# Revit family: Мембранный редуктор давления с крышкой фильтрующего элемента из прозрачного пластика 2682
name_source: partatom
category: Rohrzubehör
units: mm (PartAtom-declared; Revit-internal decimal feet)

## family parameters
Arbeitsebenenbasiert = Nein
Beim Laden mit Abzugskörper schneiden = Nein
Bemaßung runder Anschluss = Durchmesser verwenden
Gemeinsam genutzt = Nein
Immer vertikal = Ja
OmniClass-Nummer = 23.65.55.14
OmniClass-Titel = Valves for Liquid Services
Teiletyp = Unterbricht

## types (2) — shared parameters
B02 = 26 mm  [stored 0.0853018 ft]
B03 = 5 mm  [stored 0.0164042 ft]
Hersteller = HERZ Armaturen Ges.m.b.H.
R06 = 19.5 mm  [stored 0.0639764 ft]
S02 = 10 mm  [stored 0.0328084 ft]
SCTWCODE = 04;24;02
SCTWSEQ = AW;SBT_TYP_AW="111";2
URL = www.herz-armaturen.ru
W01 = 91.00°
Букса = PA6.6
Диапазон настройки выходного давления = 1.5 - 6 bar
Заводская настройка давления на выходе = 300000.0 Pa
Корпус (DN15-DN25) = штампованная латунь (EN 12165; CW626N)
Корпус (DN32-DN50) = литая латунь (EN 1982; CC770S)
Крышка = пластик PA12, прозрачный
Макс. давление на входе = 1600000.0 Pa
Макс. рабочая температура = 40 °C
Маховик = пластик PA6.6, зеленого цвета
Мембрана = EPDM
Направляющая пружины = нержавеющая сталь
Наружная резьба подключения = в соответствии с ISO 7-1 и ISO228
Область применения = Мембранный редуктор давления защищает установки от избыточного давления (снижает давление на входе до рабочего уровня).
Редуктор также может использоваться в системах отопления для защиты водонагревателя от высокого давления.
Давление на выходе настраивается в указанном диапазоне и не зависит от изменения давления на входе.
Давление на выходе можно регулировать путем поворота зеленого маховика. 
При повороте маховика по часовой стрелке увеличивается давление на выходе.
Превышение значений, указанных на шкале редуктора, может привести к повреждению устройства.
Для систем в частных домах рекомендуется установить давление на выходе равным 4 бара, что обеспечивает длительный срок службы изделия и низкие затраты во время его эксплуатации.
После изменения настройки необходимо открыть и затем закрыть водоразборный кран и далее проконтролировать достигнутое значение настроенного давления по манометру при закрытом кране водоразбора.
Подключение манометра (с обеих сторон) = 1/4" F (ISO 228-1)
Примечание = В соответствии со статьей 33 Регламента REACH (Registration; Evaluation; Authorisation; Restriction of Chemicals) (EC № 1907/2006) мы обязаны указать, что свинец внесен в список SVHC (Substances of Very High Concern - вещества очень высокой важности) и весовой процент свинца во всех латунных компонентах заводского изготовления в наших изделиях, превышает 0,1 % (w/w) (CAS: 7439-92-1 / EINECS: 231-100-4).
Поскольку свинец является легирующим компонентом сплава, прямое негативное влияние исключается, и поэтому дополнительной информации о безопасном использовании не требуется.
Пружина = пружинная сталь
Соединение "американка" = латунь CW617N
Среда = Питьевая вода
Стандарт = EN 1567
Уплотнение в мембранном редукторе = EPDM
Уплотнение соединения "американка" = Klingersil C-4324
Фильтрующий элемент = нержавеющая сталь, размер ячейки 0.3 мм
Шкала манометра = 0 - 10 bar
zero-valued in all types: SC_NennweiteBerechnet, Vorgabe-Ansicht

## type names (no varying parameters)
- Манометр спереди
- Манометр сзади

note: [stored X ft] marks values corroborated as IEEE doubles in the binary element streams (Revit-internal decimal feet)

## geometry (parser evidence)
native form markers: Extrusion x1
no freeform markers — native parametric forms only
